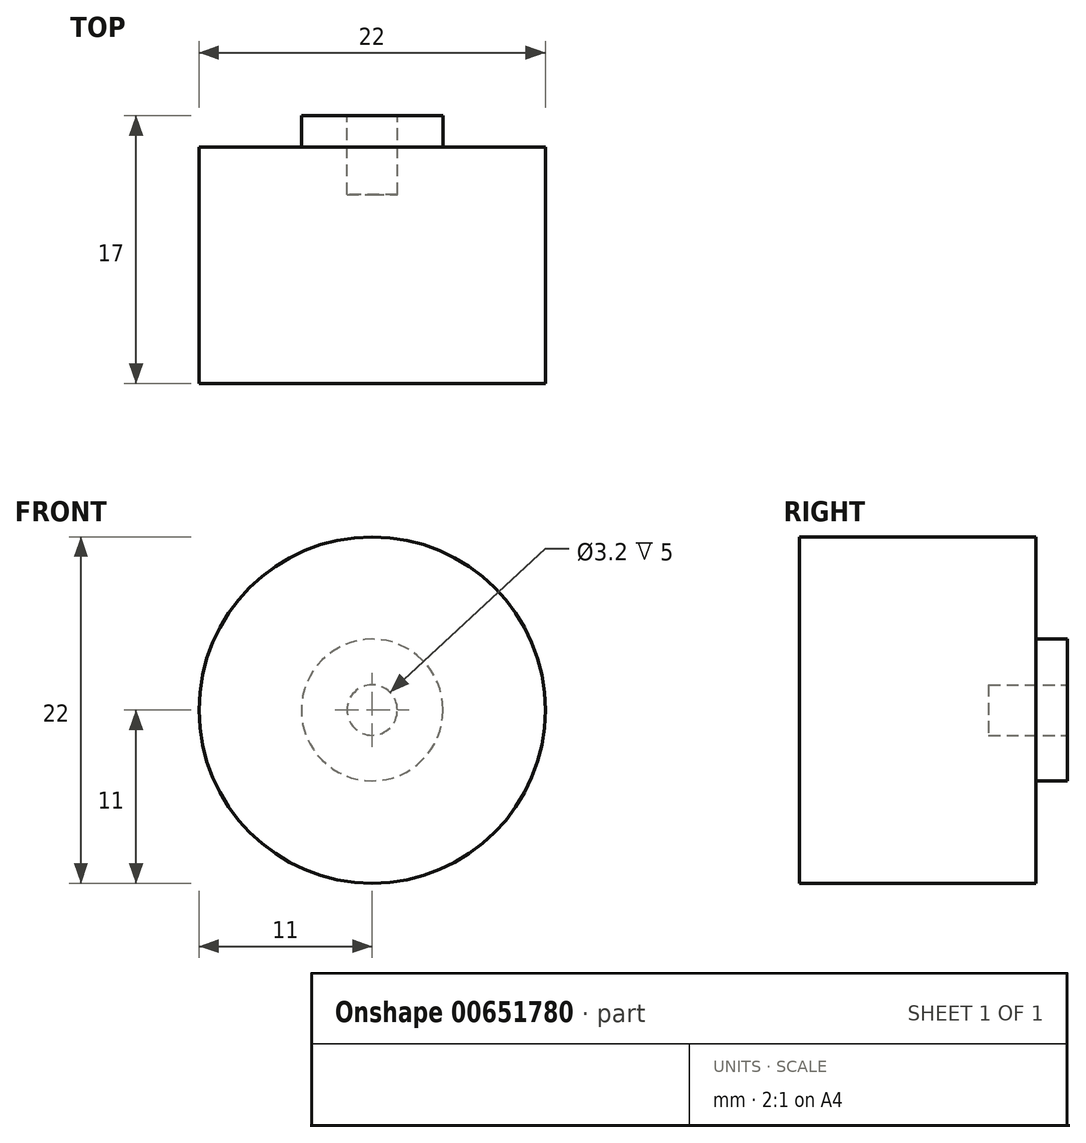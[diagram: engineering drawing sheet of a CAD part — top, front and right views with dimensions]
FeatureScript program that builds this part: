
annotation { "Feature Type Name" : "Feature", "Feature Type Description" : "" }
export const myFeature = defineFeature(function(context is Context, id is Id, definition is map)
    precondition{}
    {
        {
            var Q0;
            Q0=qCreatedBy(makeId("Front.planeOp"),FACE);
            var sketch = newSketch(context, id + "F0", { "sketchPlane" : qUnion([Q0])});
            skCircle(sketch, "E0", {"center": v(0, 0) * mm, "radius": 11 * mm});
            skSolve(sketch);
        }
        {
            var Q0;
            Q0 = qSketchRegion(id + "F0", true);
            extrude(context, id + "F1", {"entities" : qUnion([Q0]), "depth" : 15 * mm, "offsetDistance" : 25 * mm});
        }
        {
            var Q0;
            Q0=makeQuery(id+"F1.opExtrude","CAP_FACE",FACE,{"disambiguationData":[OSD([sQuery(id+"F0.wireOp",EDGE,"E0")])],"isStart":true});
            var sketch = newSketch(context, id + "F2", { "sketchPlane" : qUnion([Q0])});
            skCircle(sketch, "E1", {"center": v(0, 0) * mm, "radius": 10 * mm});
            skCircle(sketch, "E2", {"center": v(0, 0) * mm, "radius": 4.5 * mm});
            skSolve(sketch);
        }
        {
            var Q0;
            Q0=makeQuery(id+"F2.imprint","IMPRINT",FACE,{"disambiguationData":[TD([[makeQuery(id+"F2.imprint","IMPRINT",EDGE,{"derivedFrom":sQuery(id+"F2.wireOp",EDGE,"E2")}),1.0]])]});
            extrude(context, id + "F3", {"entities" : qUnion([Q0]), "operationType" : NewBodyOperationType.ADD, "depth" : 2 * mm, "offsetDistance" : 25 * mm});
        }
        {
            var Q0;
            Q0=makeQuery(id+"F3.opExtrude","CAP_FACE",FACE,{"disambiguationData":[OSD([sQuery(id+"F2.wireOp",EDGE,"E2")])],"isStart":false});
            var sketch = newSketch(context, id + "F4", { "sketchPlane" : qUnion([Q0])});
            skCircle(sketch, "E3", {"center": v(0, 0) * mm, "radius": 1.6 * mm});
            skSolve(sketch);
        }
        {
            var Q0;
            Q0=makeQuery(id+"F4.imprint","IMPRINT",FACE,{"disambiguationData":[TD([[makeQuery(id+"F4.imprint","IMPRINT",EDGE,{"derivedFrom":sQuery(id+"F4.wireOp",EDGE,"E3")}),1.0]])]});
            extrude(context, id + "F5", {"entities" : qUnion([Q0]), "operationType" : NewBodyOperationType.REMOVE, "oppositeDirection" : true, "depth" : 5 * mm, "offsetDistance" : 25 * mm});
        }
    });
